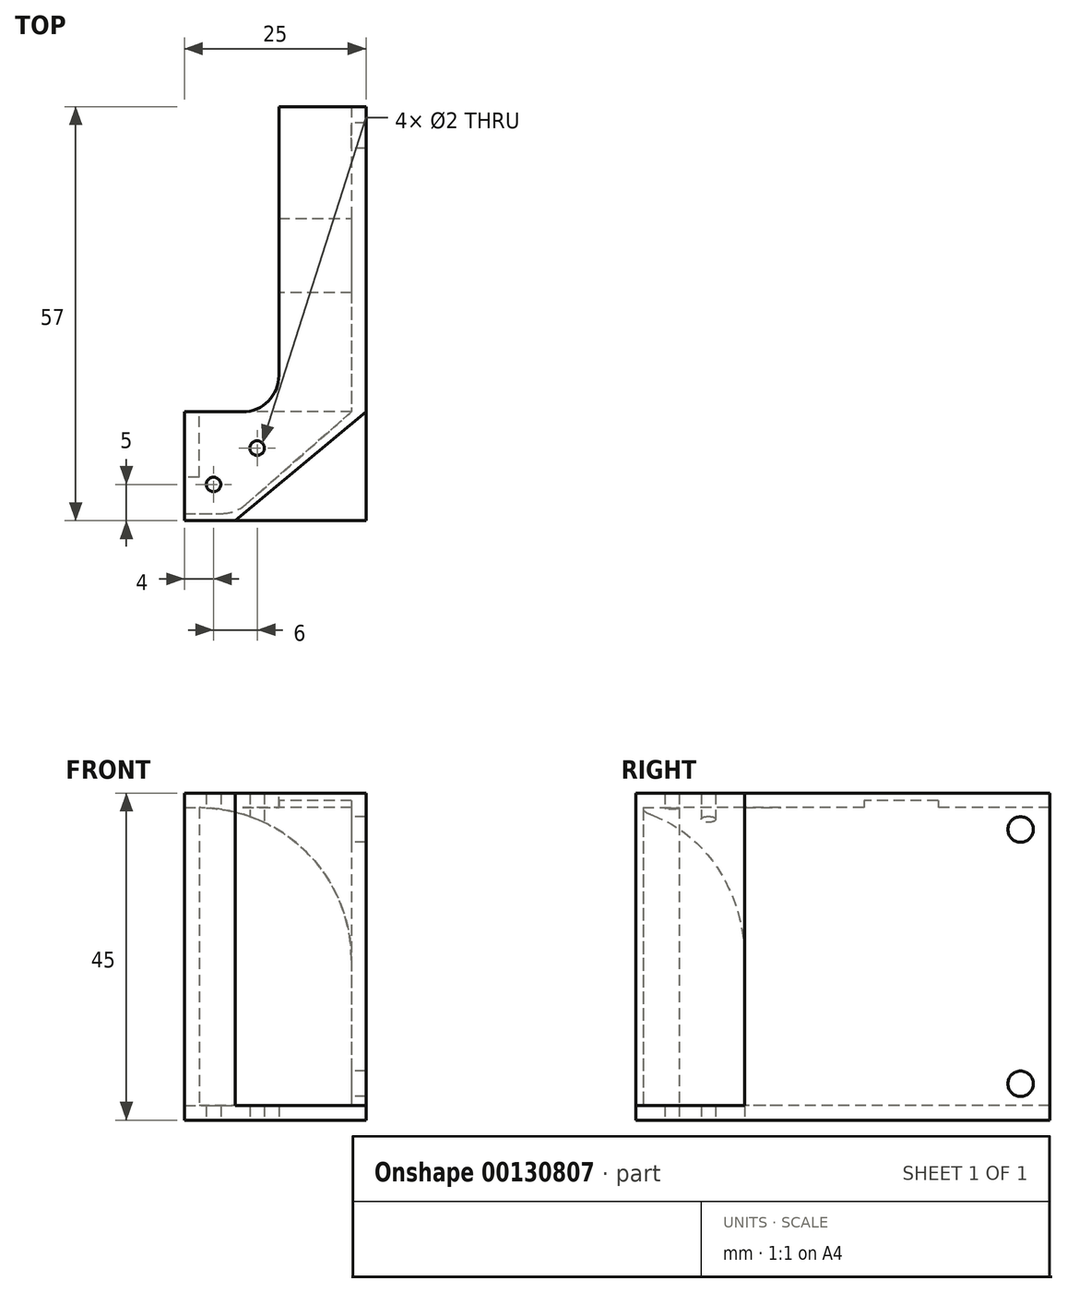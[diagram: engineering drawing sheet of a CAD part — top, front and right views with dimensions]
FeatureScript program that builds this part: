
annotation { "Feature Type Name" : "Feature", "Feature Type Description" : "" }
export const myFeature = defineFeature(function(context is Context, id is Id, definition is map)
    precondition{}
    {
        {
            var Q0;
            Q0=qCreatedBy(makeId("Top.planeOp"),FACE);
            var sketch = newSketch(context, id + "F0", { "sketchPlane" : qUnion([Q0])});
            skLineSegment(sketch, "E0", {"start": v(12, 0) * mm, "end": v(12, -42) * mm});
            skLineSegment(sketch, "E1", {"start": v(10, 0) * mm, "end": v(10, -42) * mm});
            skLineSegment(sketch, "E2", {"start": v(-13, -57) * mm, "end": v(-13, -56) * mm});
            skLineSegment(sketch, "E3", {"start": v(10, 0) * mm, "end": v(12, 0) * mm});
            skLineSegment(sketch, "E4.bottom", {"start": v(-13, -57) * mm, "end": v(-6, -57) * mm});
            skLineSegment(sketch, "E4.top", {"start": v(-13, -56) * mm, "end": v(-7.88, -56) * mm});
            skLineSegment(sketch, "E4.right", {"start": v(-6, -57) * mm, "end": v(-6, -56) * mm});
            skLineSegment(sketch, "E5", {"start": v(-4.59, -54.76) * mm, "end": v(10, -42) * mm});
            skLineSegment(sketch, "E6", {"start": v(-6, -57) * mm, "end": v(12, -42) * mm});
            skPoint(sketch, "E7.visualSharp", {"position": v(-6, -56) * mm});
            skArc(sketch, "E7.filletArc", {"start": v(-7.88, -56) * mm, "mid": v(-6.12, -55.68) * mm, "end": v(-4.59, -54.76) * mm});
            skSolve(sketch);
        }
        {
            var Q0;
            Q0=makeQuery(id+"F0.imprint","IMPRINT",FACE,{"disambiguationData":[TD([[makeQuery(id+"F0.imprint","IMPRINT",EDGE,{"derivedFrom":sQuery(id+"F0.wireOp",EDGE,"j6WAzml5-UMf8-BwAd-VWvM-0eq8f6lidWRz.bottom")}),-1.0]])]});
            var Q1;
            {var subQ0=sQuery(id+"F0.wireOp",EDGE,"SCWSvQnW-zgxt-xv1m-XBCz-Pb8vfzgxZMeU");Q1=makeQuery(id+"F0.imprint","IMPRINT",FACE,{"disambiguationData":[TD([[makeQuery(id+"F0.imprint","IMPRINT",EDGE,{"derivedFrom":subQ0}),-1.0]])]});}
            var Q2;
            Q2=makeQuery(id+"F0.imprint","IMPRINT",FACE,{"disambiguationData":[TD([[makeQuery(id+"F0.imprint","IMPRINT",EDGE,{"derivedFrom":sQuery(id+"F0.wireOp",EDGE,"E0")}),-1.0]])]});
            extrude(context, id + "F1", {"entities" : qUnion([Q0, Q1, Q2]), "depth" : 45 * mm});
        }
        {
            var Q0;
            Q0=makeQuery(id+"F1.opExtrude","SWEPT_FACE",FACE,{"disambiguationData":[OSD([sQuery(id+"F0.wireOp",EDGE,"E1")])]});
            var sketch = newSketch(context, id + "F2", { "sketchPlane" : qUnion([Q0])});
            skCircle(sketch, "E8", {"center": v(4, 5) * mm, "radius": 1.75 * mm});
            skCircle(sketch, "E9", {"center": v(4, 40) * mm, "radius": 1.75 * mm});
            skLineSegment(sketch, "E10", {"start": v(4, 5) * mm, "end": v(4, 40) * mm});
            skPoint(sketch, "E11.startSnap0", {"position": v(0, 22.5) * mm});
            skPoint(sketch, "E11.startSnap1", {"position": v(4, 22.5) * mm});
            skPoint(sketch, "E11.endSnap0", {"position": v(0, 22.5) * mm});
            skPoint(sketch, "E11.endSnap1", {"position": v(4, 22.5) * mm});
            skSolve(sketch);
        }
        {
            var Q0;
            Q0=qSketchRegion(id+"F2",true);
            extrude(context, id + "F3", {"entities" : qUnion([Q0]), "operationType" : NewBodyOperationType.REMOVE, "endBound" : BoundingType.UP_TO_NEXT, "oppositeDirection" : true, "depth" : 25 * mm});
        }
        {
            var Q0;
            Q0=makeQuery(id+"F1.opExtrude","CAP_FACE",FACE,{"disambiguationData":[OSD([sQuery(id+"F0.wireOp",EDGE,"j6WAzml5-UMf8-BwAd-VWvM-0eq8f6lidWRz.bottom"),sQuery(id+"F0.wireOp",EDGE,"j6WAzml5-UMf8-BwAd-VWvM-0eq8f6lidWRz.top"),sQuery(id+"F0.wireOp",EDGE,"j6WAzml5-UMf8-BwAd-VWvM-0eq8f6lidWRz.left"),sQuery(id+"F0.wireOp",EDGE,"E0"),sQuery(id+"F0.wireOp",EDGE,"E1"),sQuery(id+"F0.wireOp",EDGE,"SCWSvQnW-zgxt-xv1m-XBCz-Pb8vfzgxZMeU"),sQuery(id+"F0.wireOp",EDGE,"5fDDolJY-3XqT-nJg0-wMJl-OrCj20yJezuh"),sQuery(id+"F0.wireOp",EDGE,"Il1p7j2H-3KLv-yJme-Qiy4-S6na7ejKmFE0"),sQuery(id+"F0.wireOp",EDGE,"prwiAy6F-z69O-hduv-U2qo-wSjXJho67qsL")])],"isStart":true});
            var sketch = newSketch(context, id + "F4", { "sketchPlane" : qUnion([Q0])});
            skLineSegment(sketch, "E12", {"start": v(12, 42) * mm, "end": v(12, 0) * mm});
            skLineSegment(sketch, "E13.left", {"start": v(12, 0) * mm, "end": v(12, 42) * mm});
            skPoint(sketch, "E14.endSnap0", {"position": v(12, 21) * mm});
            skLineSegment(sketch, "E15", {"start": v(0, 0) * mm, "end": v(12, 0) * mm});
            skLineSegment(sketch, "E16", {"start": v(0, 0) * mm, "end": v(0, 52) * mm});
            skLineSegment(sketch, "E17", {"start": v(0, 52) * mm, "end": v(12, 42) * mm});
            skLineSegment(sketch, "E18", {"start": v(10, 42) * mm, "end": v(-13, 42) * mm});
            skLineSegment(sketch, "E19", {"start": v(-13, 42) * mm, "end": v(-13, 57) * mm});
            skLineSegment(sketch, "E20", {"start": v(-13, 57) * mm, "end": v(-6, 57) * mm});
            skLineSegment(sketch, "E21", {"start": v(-6, 57) * mm, "end": v(12, 42) * mm});
            skLineSegment(sketch, "E22", {"start": v(10, 42) * mm, "end": v(12, 42) * mm});
            skCircle(sketch, "E23", {"center": v(-9, 52) * mm, "radius": 1 * mm});
            skCircle(sketch, "E24", {"center": v(-3, 47) * mm, "radius": 1 * mm});
            skLineSegment(sketch, "E25", {"start": v(12, 42) * mm, "end": v(12, 57) * mm});
            skLineSegment(sketch, "E26", {"start": v(12, 57) * mm, "end": v(-6, 57) * mm});
            skSolve(sketch);
        }
        {
            var Q0;
            {var subQ0=sQuery(id+"F4.wireOp",EDGE,"Pp7L3Jzv-O3kp-prUG-vLfv-zSUn7I2e2rIo");Q0=makeQuery(id+"F4.imprint","IMPRINT",FACE,{"disambiguationData":[TD([[makeQuery(id+"F4.imprint","IMPRINT",EDGE,{"derivedFrom":subQ0}),-1.0]])]});}
            var Q1;
            {var subQ3=makeQuery(id+"F1.opExtrude","CAP_EDGE",EDGE,{"disambiguationData":[OSD([sQuery(id+"F0.wireOp",EDGE,"E1")])],"isStart":true});var subQ5=makeQuery(id+"F1.opExtrude","CAP_EDGE",EDGE,{"disambiguationData":[OSD([sQuery(id+"F0.wireOp",EDGE,"j6WAzml5-UMf8-BwAd-VWvM-0eq8f6lidWRz.top")])],"isStart":true});var subQ7=makeQuery(id+"F4.imprint","INTERSECT",VERTEX,{"derivedFrom":[subQ5,subQ3]});Q1=makeQuery(id+"F4.imprint","IMPRINT",FACE,{"disambiguationData":[TD([[makeQuery(id+"F4.imprint","IMPRINT",EDGE,{"disambiguationData":[TD([[subQ7,1.0]])],"derivedFrom":subQ5}),1.0]])]});}
            var Q2;
            {var subQ1=sQuery(id+"F4.wireOp",EDGE,"kJNlpIVx-vw54-H6Pj-ckVB-lwE8ZodcR6sP");Q2=makeQuery(id+"F4.imprint","IMPRINT",FACE,{"disambiguationData":[TD([[makeQuery(id+"F4.imprint","IMPRINT",EDGE,{"derivedFrom":subQ1}),-1.0]])]});}
            var Q3;
            {var subQ0=sQuery(id+"F4.wireOp",EDGE,"E14");var subQ1=sQuery(id+"F4.wireOp",EDGE,"E13.right");var subQ2=makeQuery(id+"F4.imprint","INTERSECT",VERTEX,{"derivedFrom":[subQ1,subQ0]});Q3=makeQuery(id+"F4.imprint","IMPRINT",FACE,{"disambiguationData":[TD([[makeQuery(id+"F4.imprint","IMPRINT",EDGE,{"disambiguationData":[TD([[subQ2,1.0]])],"derivedFrom":subQ1}),-1.0]])]});}
            var Q4;
            {var subQ1=sQuery(id+"F4.wireOp",EDGE,"E13.top");var subQ3=makeQuery(id+"F1.opExtrude","CAP_EDGE",EDGE,{"disambiguationData":[OSD([sQuery(id+"F0.wireOp",EDGE,"E1")])],"isStart":true});var subQ4=makeQuery(id+"F4.imprint","INTERSECT",VERTEX,{"derivedFrom":[subQ3,subQ1]});Q4=makeQuery(id+"F4.imprint","IMPRINT",FACE,{"disambiguationData":[TD([[makeQuery(id+"F4.imprint","IMPRINT",EDGE,{"disambiguationData":[TD([[subQ4,-1.0]])],"derivedFrom":subQ1}),1.0]])]});}
            var Q5;
            {var subQ0=sQuery(id+"F4.wireOp",EDGE,"8FUNc06l-UDnM-y1Sg-Qo9e-B5HObuIuT9JA");Q5=makeQuery(id+"F4.imprint","IMPRINT",FACE,{"disambiguationData":[TD([[makeQuery(id+"F4.imprint","IMPRINT",EDGE,{"derivedFrom":subQ0}),-1.0]])]});}
            var Q6;
            {var subQ0=sQuery(id+"F4.wireOp",EDGE,"E18");var subQ1=sQuery(id+"F4.wireOp",EDGE,"E16");var subQ2=makeQuery(id+"F4.imprint","INTERSECT",VERTEX,{"derivedFrom":[subQ1,subQ0]});Q6=makeQuery(id+"F4.imprint","IMPRINT",FACE,{"disambiguationData":[TD([[makeQuery(id+"F4.imprint","IMPRINT",EDGE,{"disambiguationData":[TD([[subQ2,-1.0]])],"derivedFrom":subQ1}),-1.0]])]});}
            var Q7;
            {var subQ0=makeQuery(id+"F1.opExtrude","CAP_EDGE",EDGE,{"disambiguationData":[OSD([sQuery(id+"F0.wireOp",EDGE,"E4.top")])],"isStart":true});Q7=makeQuery(id+"F4.imprint","IMPRINT",FACE,{"disambiguationData":[TD([[makeQuery(id+"F4.imprint","IMPRINT",EDGE,{"derivedFrom":subQ0}),-1.0]])]});}
            var Q8;
            {var subQ0=sQuery(id+"F4.wireOp",EDGE,"E17");Q8=makeQuery(id+"F4.imprint","IMPRINT",FACE,{"disambiguationData":[TD([[makeQuery(id+"F4.imprint","IMPRINT",EDGE,{"derivedFrom":subQ0}),-1.0]])]});}
            var Q9;
            {var subQ0=sQuery(id+"F4.wireOp",EDGE,"E17");Q9=makeQuery(id+"F4.imprint","IMPRINT",FACE,{"disambiguationData":[TD([[makeQuery(id+"F4.imprint","IMPRINT",EDGE,{"derivedFrom":subQ0}),1.0]])]});}
            var Q10;
            {var subQ1=makeQuery(id+"F1.opExtrude","CAP_EDGE",EDGE,{"disambiguationData":[OSD([sQuery(id+"F0.wireOp",EDGE,"E1")])],"isStart":true});Q10=makeQuery(id+"F4.imprint","IMPRINT",FACE,{"disambiguationData":[TD([[makeQuery(id+"F4.imprint","IMPRINT",EDGE,{"derivedFrom":subQ1}),1.0]])]});}
            var Q11;
            Q11=makeQuery(id+"F4.imprint","IMPRINT",FACE,{"disambiguationData":[TD([[makeQuery(id+"F4.imprint","IMPRINT",EDGE,{"derivedFrom":sQuery(id+"F4.wireOp",EDGE,"E24")}),1.0]])]});
            var Q12;
            Q12=makeQuery(id+"F4.imprint","IMPRINT",FACE,{"disambiguationData":[TD([[makeQuery(id+"F4.imprint","IMPRINT",EDGE,{"derivedFrom":sQuery(id+"F4.wireOp",EDGE,"E23")}),1.0]])]});
            extrude(context, id + "F5", {"entities" : qUnion([Q0, Q1, Q2, Q3, Q4, Q5, Q6, Q7, Q8, Q9, Q10, Q11, Q12]), "operationType" : NewBodyOperationType.ADD, "oppositeDirection" : true, "depth" : 2 * mm});
        }
        {
            var Q0;
            {var subQ0=sQuery(id+"F0.wireOp",EDGE,"E1");var subQ1=sQuery(id+"F0.wireOp",EDGE,"E0");var subQ2=sQuery(id+"F0.wireOp",EDGE,"j6WAzml5-UMf8-BwAd-VWvM-0eq8f6lidWRz.top");var subQ3=sQuery(id+"F0.wireOp",EDGE,"prwiAy6F-z69O-hduv-U2qo-wSjXJho67qsL");var subQ4=sQuery(id+"F0.wireOp",EDGE,"j6WAzml5-UMf8-BwAd-VWvM-0eq8f6lidWRz.bottom");var subQ5=sQuery(id+"F0.wireOp",EDGE,"SCWSvQnW-zgxt-xv1m-XBCz-Pb8vfzgxZMeU");var subQ6=sQuery(id+"F0.wireOp",EDGE,"5fDDolJY-3XqT-nJg0-wMJl-OrCj20yJezuh");var subQ7=sQuery(id+"F0.wireOp",EDGE,"Il1p7j2H-3KLv-yJme-Qiy4-S6na7ejKmFE0");Q0=makeQuery(id+"F9wXORycC4JNOCb_1.boolean.opBoolean","SPLIT",FACE,{"disambiguationData":[TD([makeQuery(id+"F1.opExtrude","SWEPT_FACE",FACE,{"disambiguationData":[OSD([subQ4])]}),makeQuery(id+"F1.opExtrude","SWEPT_FACE",FACE,{"disambiguationData":[OSD([subQ2])]}),makeQuery(id+"F1.opExtrude","SWEPT_FACE",FACE,{"disambiguationData":[OSD([subQ1])]}),makeQuery(id+"F1.opExtrude","SWEPT_FACE",FACE,{"disambiguationData":[OSD([subQ0])]}),makeQuery(id+"F1.opExtrude","SWEPT_FACE",FACE,{"disambiguationData":[OSD([subQ5])]}),makeQuery(id+"F1.opExtrude","SWEPT_FACE",FACE,{"disambiguationData":[OSD([subQ6])]}),makeQuery(id+"F1.opExtrude","SWEPT_FACE",FACE,{"disambiguationData":[OSD([subQ7])]}),makeQuery(id+"F1.opExtrude","SWEPT_FACE",FACE,{"disambiguationData":[OSD([subQ3])]}),makeQuery(id+"F9wXORycC4JNOCb_1.opExtrude","SWEPT_FACE",FACE,{"disambiguationData":[OSD([sQuery(id+"FcY7FGCUkcGvyBp_1.wireOp",EDGE,"cLe4Pgn2-JyEj-5vE0-BmVZ-GLZ1qCNQxqep")])]})])],"derivedFrom":makeQuery(id+"F1.opExtrude","CAP_FACE",FACE,{"disambiguationData":[OSD([subQ4,subQ2,sQuery(id+"F0.wireOp",EDGE,"j6WAzml5-UMf8-BwAd-VWvM-0eq8f6lidWRz.left"),subQ1,subQ0,subQ5,subQ6,subQ7,subQ3])],"isStart":false})});}
            var sketch = newSketch(context, id + "F6", { "sketchPlane" : qUnion([Q0])});
            skLineSegment(sketch, "E27", {"start": v(12, 0) * mm, "end": v(0, 0) * mm});
            skLineSegment(sketch, "E28", {"start": v(0, 0) * mm, "end": v(0, -42) * mm});
            skLineSegment(sketch, "E29", {"start": v(0, -42) * mm, "end": v(-13, -42) * mm});
            skLineSegment(sketch, "E30", {"start": v(-13, -42) * mm, "end": v(-13, -57) * mm});
            skLineSegment(sketch, "E31", {"start": v(-13, -57) * mm, "end": v(-6, -57) * mm});
            skLineSegment(sketch, "E32", {"start": v(12, -42) * mm, "end": v(12, 0) * mm});
            skLineSegment(sketch, "E33", {"start": v(-6, -57) * mm, "end": v(12, -42) * mm});
            skSolve(sketch);
        }
        {
            var Q0;
            Q0=qSketchRegion(id+"F6",true);
            extrude(context, id + "F7", {"entities" : qUnion([Q0]), "operationType" : NewBodyOperationType.ADD, "oppositeDirection" : true, "depth" : 2 * mm});
        }
        {
            var Q0;
            Q0=makeQuery(id+"F7.opExtrude","SWEPT_EDGE",EDGE,{"disambiguationData":[OSD([sQuery(id+"F6.wireOp",EDGE,"E28"),sQuery(id+"F6.wireOp",EDGE,"E29")])]});
            var Q1;
            Q1=makeQuery(id+"F5.opExtrude","SWEPT_EDGE",EDGE,{"disambiguationData":[OSD([sQuery(id+"F4.wireOp",EDGE,"E16"),sQuery(id+"F4.wireOp",EDGE,"E18")])]});
            fillet(context, id + "F8", {"entities" : qUnion([Q0, Q1]), "radius" : 5 * mm, "tangentPropagation" : true, "allowEdgeOverflow" : false});
        }
        {
            var Q0;
            {var subQ0=sQuery(id+"F6.wireOp",EDGE,"E27");var subQ1=sQuery(id+"F6.wireOp",EDGE,"E28");var subQ2=sQuery(id+"F6.wireOp",EDGE,"E29");var subQ3=sQuery(id+"F6.wireOp",EDGE,"E30");Q0=makeQuery(id+"F7.boolean.opBoolean","SPLIT",FACE,{"disambiguationData":[TD([makeQuery(id+"F1.opExtrude","SWEPT_FACE",FACE,{"disambiguationData":[OSD([sQuery(id+"F0.wireOp",EDGE,"E1")])]})])],"derivedFrom":makeQuery(id+"F7.opExtrude","CAP_FACE",FACE,{"disambiguationData":[OSD([subQ0,subQ1,subQ2,subQ3,sQuery(id+"F6.wireOp",EDGE,"E31"),sQuery(id+"F6.wireOp",EDGE,"E32")])],"isStart":false})});}
            var sketch = newSketch(context, id + "F9", { "sketchPlane" : qUnion([Q0])});
            skLineSegment(sketch, "E34.bottom", {"start": v(10, 25.58) * mm, "end": v(0, 25.58) * mm});
            skLineSegment(sketch, "E34.left", {"start": v(10, 25.58) * mm, "end": v(10, 15.37) * mm});
            skLineSegment(sketch, "E35.top", {"start": v(0, 15.37) * mm, "end": v(10, 15.37) * mm});
            skLineSegment(sketch, "E35.left", {"start": v(0, 25.58) * mm, "end": v(0, 15.37) * mm});
            skPoint(sketch, "E36.newPointB", {"position": v(5.89, 15.37) * mm});
            skSolve(sketch);
        }
        {
            var Q0;
            Q0=qSketchRegion(id+"F9",true);
            extrude(context, id + "F10", {"entities" : qUnion([Q0]), "operationType" : NewBodyOperationType.REMOVE, "oppositeDirection" : true, "depth" : 1 * mm});
        }
        {
            var Q0;
            Q0=makeQuery(id+"F7.boolean.opBoolean","MERGE",FACE,{"derivedFrom":[makeQuery(id+"F5.boolean.opBoolean","MERGE",FACE,{"derivedFrom":[makeQuery(id+"F1.opExtrude","SWEPT_FACE",FACE,{"disambiguationData":[OSD([sQuery(id+"F0.wireOp",EDGE,"E2")])]}),makeQuery(id+"F5.opExtrude","SWEPT_FACE",FACE,{"disambiguationData":[OSD([sQuery(id+"F4.wireOp",EDGE,"E19")])]})]}),makeQuery(id+"F7.opExtrude","SWEPT_FACE",FACE,{"disambiguationData":[OSD([sQuery(id+"F6.wireOp",EDGE,"E30")])]})]});
            var sketch = newSketch(context, id + "F11", { "sketchPlane" : qUnion([Q0])});
            skLineSegment(sketch, "E37.bottom", {"start": v(42, 45) * mm, "end": v(51, 45) * mm});
            skLineSegment(sketch, "E37.top", {"start": v(42, 0) * mm, "end": v(51, 0) * mm});
            skLineSegment(sketch, "E37.left", {"start": v(42, 45) * mm, "end": v(42, 0) * mm});
            skLineSegment(sketch, "E37.right", {"start": v(51, 45) * mm, "end": v(51, 0) * mm});
            skSolve(sketch);
        }
        {
            var Q0;
            {var subQ0=sQuery(id+"F11.wireOp",EDGE,"E37.left");var subQ1=makeQuery(id+"F5.opExtrude","CAP_EDGE",EDGE,{"disambiguationData":[OSD([sQuery(id+"F4.wireOp",EDGE,"5eHKc6lS-FkIN-35iW-rQgv-hf9qaClxwCS6")])],"isStart":false});var subQ2=makeQuery(id+"F11.imprint","INTERSECT",VERTEX,{"derivedFrom":[subQ1,subQ0]});Q0=makeQuery(id+"F11.imprint","IMPRINT",FACE,{"disambiguationData":[TD([[makeQuery(id+"F11.imprint","IMPRINT",EDGE,{"disambiguationData":[TD([[subQ2,1.0]])],"derivedFrom":subQ0}),1.0]])]});}
            extrude(context, id + "F12", {"entities" : qUnion([Q0]), "operationType" : NewBodyOperationType.ADD, "oppositeDirection" : true, "depth" : 2 * mm});
        }
        {
            var Q0;
            Q0=qCreatedBy(makeId("Front.planeOp"),FACE);
            cPlane(context, id + "F13", {"entities" : qUnion([Q0]), "cplaneType" : CPlaneType.OFFSET, "offset" : 42 * mm, "width" : 150 * mm, "height" : 150 * mm});
        }
        {
            var Q0;
            Q0=qCreatedBy(id+"F13.planeOp",FACE);
            var sketch = newSketch(context, id + "F14", { "sketchPlane" : qUnion([Q0])});
            skArc(sketch, "E38", {"start": v(10, 22) * mm, "mid": v(3.85, 36.85) * mm, "end": v(-11, 43) * mm});
            skLineSegment(sketch, "E39", {"start": v(10, 22) * mm, "end": v(10, 43) * mm});
            skLineSegment(sketch, "E40", {"start": v(10, 43) * mm, "end": v(-11, 43) * mm});
            skSolve(sketch);
        }
        {
            var Q0;
            Q0=qSketchRegion(id+"F14",true);
            extrude(context, id + "F15", {"entities" : qUnion([Q0]), "operationType" : NewBodyOperationType.ADD, "endBound" : BoundingType.UP_TO_NEXT, "depth" : 25 * mm});
        }
        {
            var Q0;
            Q0=makeQuery(id+"F4.imprint","IMPRINT",FACE,{"disambiguationData":[TD([[makeQuery(id+"F4.imprint","IMPRINT",EDGE,{"derivedFrom":sQuery(id+"F4.wireOp",EDGE,"E24")}),1.0]])]});
            var Q1;
            Q1=makeQuery(id+"F4.imprint","IMPRINT",FACE,{"disambiguationData":[TD([[makeQuery(id+"F4.imprint","IMPRINT",EDGE,{"derivedFrom":sQuery(id+"F4.wireOp",EDGE,"E23")}),1.0]])]});
            extrude(context, id + "F16", {"entities" : qUnion([Q0, Q1]), "operationType" : NewBodyOperationType.REMOVE, "endBound" : BoundingType.THROUGH_ALL, "oppositeDirection" : true, "depth" : 25 * mm});
        }
    });
